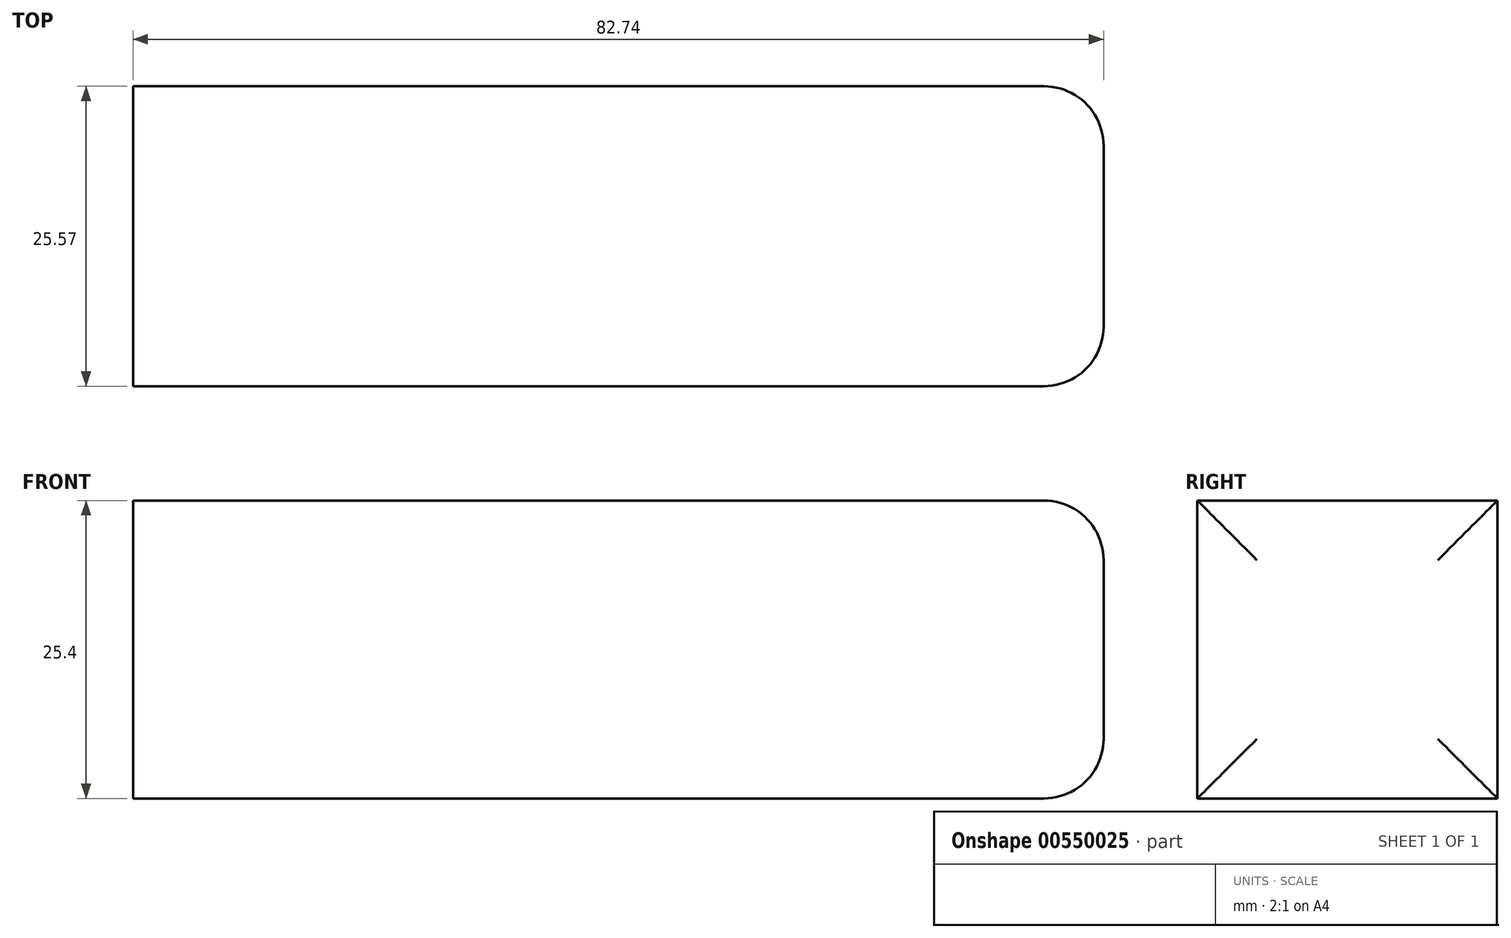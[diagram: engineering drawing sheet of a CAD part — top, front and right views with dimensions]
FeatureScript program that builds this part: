
annotation { "Feature Type Name" : "Feature", "Feature Type Description" : "" }
export const myFeature = defineFeature(function(context is Context, id is Id, definition is map)
    precondition{}
    {
        {
            var Q0;
            Q0=qCreatedBy(makeId("Top.planeOp"),FACE);
            var sketch = newSketch(context, id + "F0", { "sketchPlane" : qUnion([Q0])});
            skLineSegment(sketch, "E0.bottom", {"start": v(-19.03, 8.7) * mm, "end": v(63.71, 8.7) * mm});
            skLineSegment(sketch, "E0.top", {"start": v(-19.03, -16.88) * mm, "end": v(63.71, -16.88) * mm});
            skLineSegment(sketch, "E0.left", {"start": v(-19.03, 8.7) * mm, "end": v(-19.03, -16.88) * mm});
            skLineSegment(sketch, "E0.right", {"start": v(63.71, 8.7) * mm, "end": v(63.71, -16.88) * mm});
            skSolve(sketch);
        }
        {
            var Q0;
            Q0=makeQuery(id+"F0.imprint","IMPRINT",FACE,{"disambiguationData":[TD([[makeQuery(id+"F0.imprint","IMPRINT",EDGE,{"derivedFrom":sQuery(id+"F0.wireOp",EDGE,"E0.bottom")}),-1.0]])]});
            extrude(context, id + "F1", {"entities" : qUnion([Q0]), "depth" : 25.4 * mm, "offsetDistance" : 25.4 * mm});
        }
        {
            var Q0;
            Q0=makeQuery(id+"F1.opExtrude","SWEPT_FACE",FACE,{"disambiguationData":[OSD([sQuery(id+"F0.wireOp",EDGE,"E0.right")])]});
            fillet(context, id + "F2", {"entities" : qUnion([Q0]), "radius" : 5.08 * mm, "tangentPropagation" : true, "allowEdgeOverflow" : false});
        }
    });
